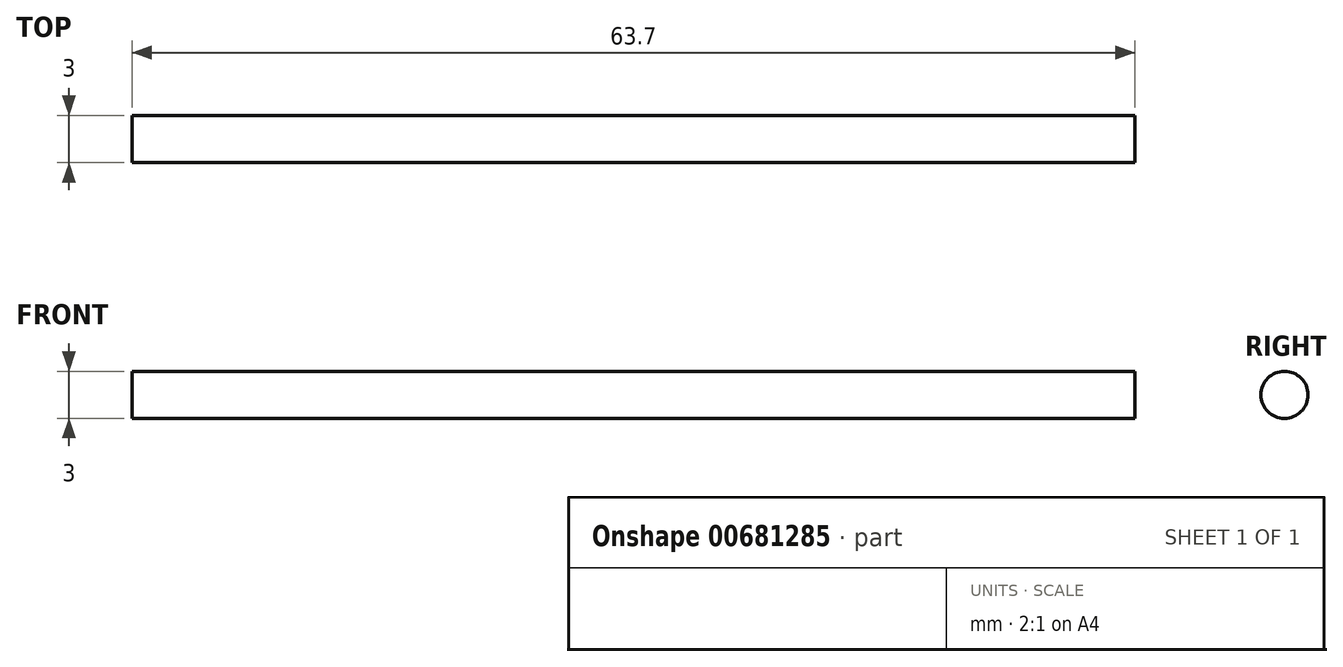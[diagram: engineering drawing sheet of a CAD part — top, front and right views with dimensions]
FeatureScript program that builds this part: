
annotation { "Feature Type Name" : "Feature", "Feature Type Description" : "" }
export const myFeature = defineFeature(function(context is Context, id is Id, definition is map)
    precondition{}
    {
        {
            var Q0;
            Q0=qCreatedBy(makeId("Right.planeOp"),FACE);
            var sketch = newSketch(context, id + "F0", { "sketchPlane" : qUnion([Q0])});
            skCircle(sketch, "E0", {"center": v(0, 0) * mm, "radius": 1.5 * mm});
            skSolve(sketch);
        }
        {
            var Q0;
            Q0 = qSketchRegion(id + "F0", true);
            extrude(context, id + "F1", {"entities" : qUnion([Q0]), "depth" : 63.7 * mm, "offsetDistance" : 25.4 * mm});
        }
    });
